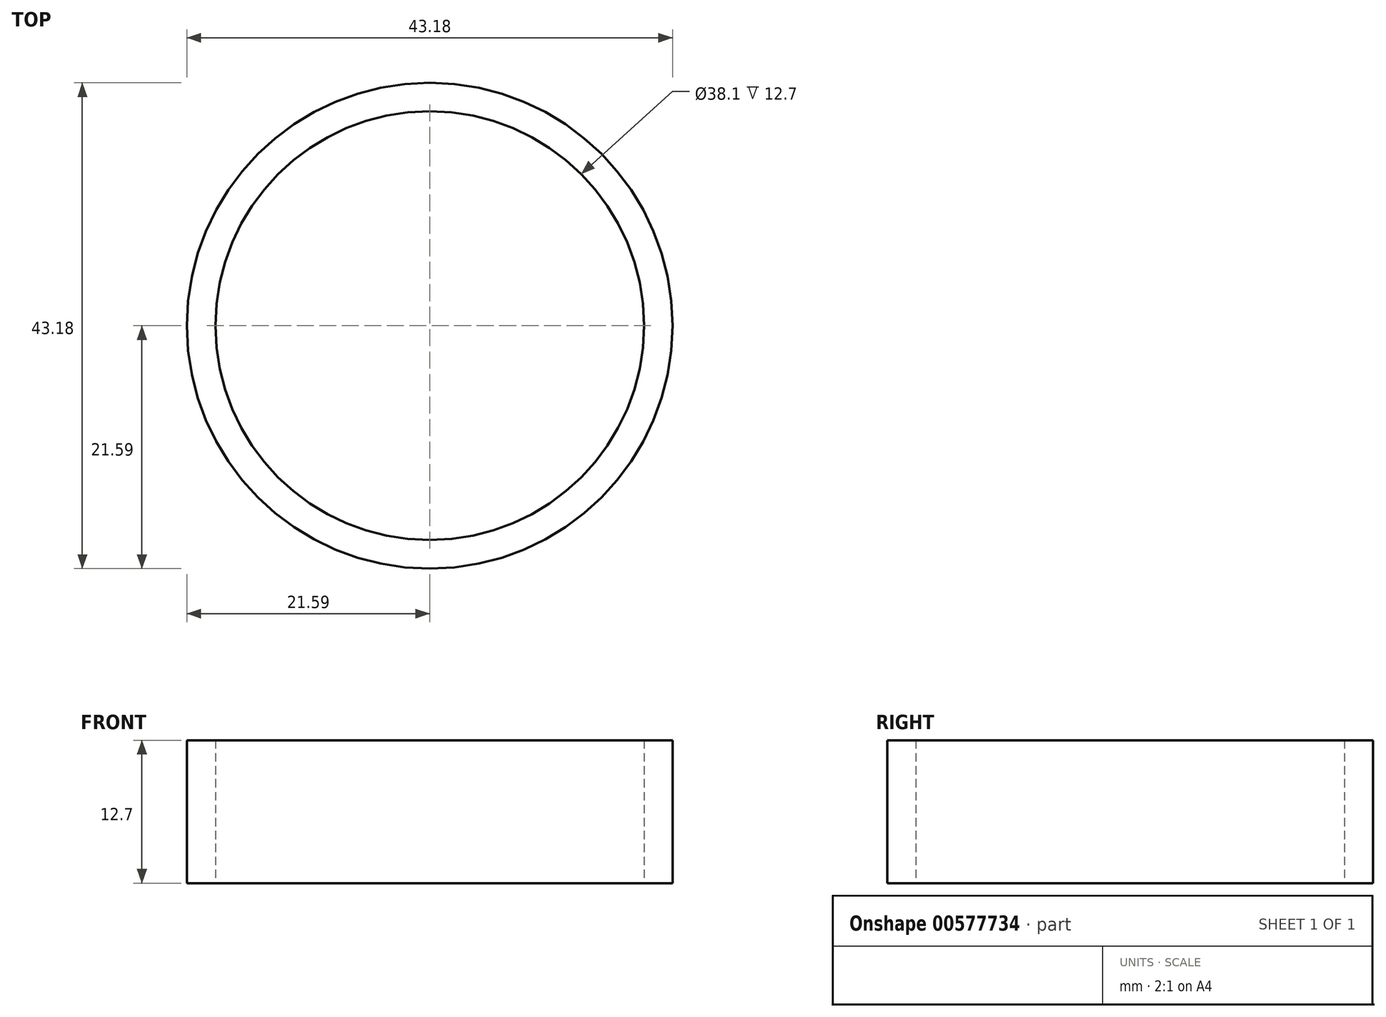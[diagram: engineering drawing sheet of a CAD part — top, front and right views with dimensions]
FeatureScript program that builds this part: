
annotation { "Feature Type Name" : "Feature", "Feature Type Description" : "" }
export const myFeature = defineFeature(function(context is Context, id is Id, definition is map)
    precondition{}
    {
        {
            var Q0;
            Q0=qCreatedBy(makeId("Top.planeOp"),FACE);
            var sketch = newSketch(context, id + "F0", { "sketchPlane" : qUnion([Q0])});
            skCircle(sketch, "E0", {"center": v(0, 0) * mm, "radius": 21.59 * mm});
            skSolve(sketch);
        }
        {
            var Q0;
            Q0=makeQuery(id+"F0.imprint","IMPRINT",FACE,{"disambiguationData":[TD([[makeQuery(id+"F0.imprint","IMPRINT",EDGE,{"derivedFrom":sQuery(id+"F0.wireOp",EDGE,"E0")}),1.0]])]});
            extrude(context, id + "F1", {"entities" : qUnion([Q0]), "depth" : 12.7 * mm, "offsetDistance" : 25.4 * mm});
        }
        {
            var Q0;
            Q0=qCreatedBy(makeId("Top.planeOp"),FACE);
            var sketch = newSketch(context, id + "F2", { "sketchPlane" : qUnion([Q0])});
            skCircle(sketch, "E1", {"center": v(0, 0) * mm, "radius": 19.05 * mm});
            skSolve(sketch);
        }
        {
            var Q0;
            Q0=makeQuery(id+"F2.imprint","IMPRINT",FACE,{"disambiguationData":[TD([[makeQuery(id+"F2.imprint","IMPRINT",EDGE,{"derivedFrom":sQuery(id+"F2.wireOp",EDGE,"E1")}),1.0]])]});
            var Q1;
            Q1=sQuery(id+"F2.wireOp",EDGE,"E1");
            extrude(context, id + "F3", {"entities" : qUnion([Q0]), "operationType" : NewBodyOperationType.REMOVE, "surfaceEntities" : qUnion([Q1]), "depth" : 50.55 * mm, "offsetDistance" : 25.4 * mm});
        }
    });
